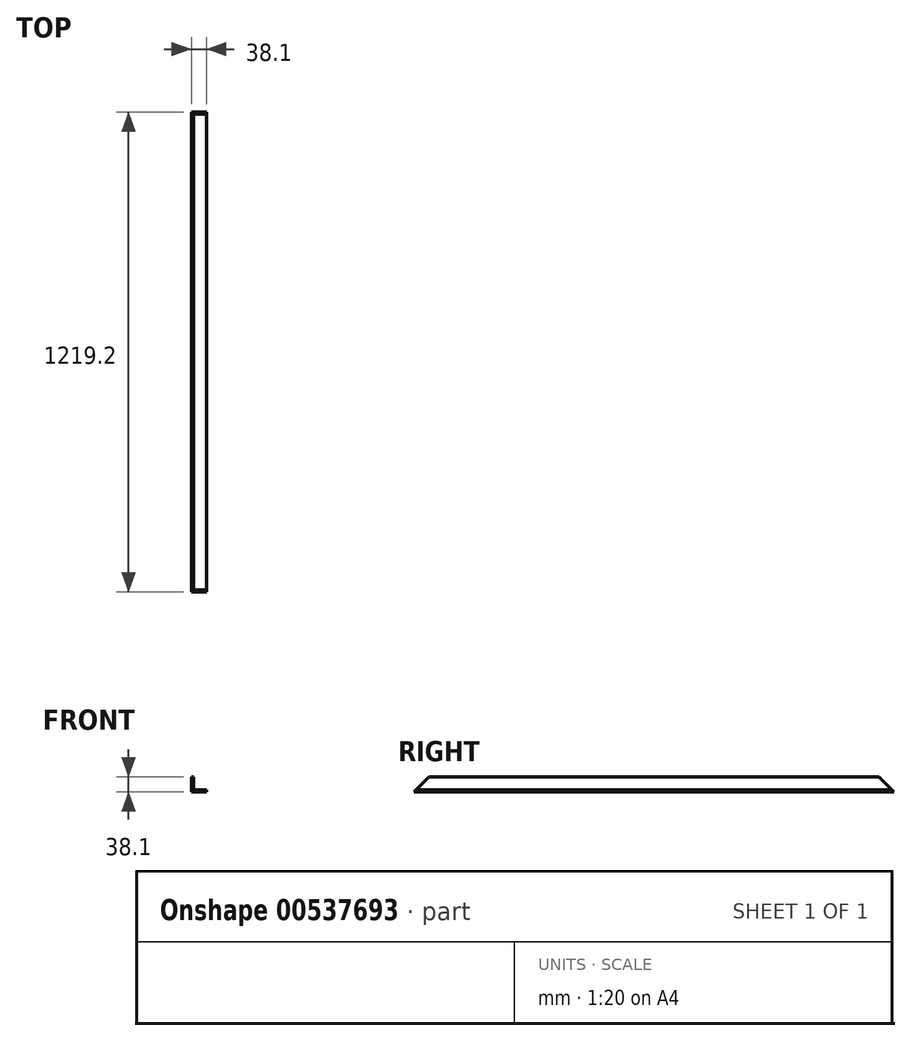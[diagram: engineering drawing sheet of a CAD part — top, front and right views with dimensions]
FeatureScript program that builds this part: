
annotation { "Feature Type Name" : "Feature", "Feature Type Description" : "" }
export const myFeature = defineFeature(function(context is Context, id is Id, definition is map)
    precondition{}
    {
        {
            var Q0;
            Q0=qCreatedBy(makeId("Front.planeOp"),FACE);
            var sketch = newSketch(context, id + "F0", { "sketchPlane" : qUnion([Q0])});
            skLineSegment(sketch, "E0", {"start": v(0, 0) * mm, "end": v(0, 38.1) * mm});
            skLineSegment(sketch, "E1", {"start": v(0, 38.1) * mm, "end": v(4.76, 38.1) * mm});
            skLineSegment(sketch, "E2", {"start": v(4.76, 38.1) * mm, "end": v(4.76, 4.76) * mm});
            skLineSegment(sketch, "E3", {"start": v(4.76, 4.76) * mm, "end": v(38.1, 4.76) * mm});
            skLineSegment(sketch, "E4", {"start": v(38.1, 4.76) * mm, "end": v(38.1, 0) * mm});
            skLineSegment(sketch, "E5", {"start": v(38.1, 0) * mm, "end": v(0, 0) * mm});
            skSolve(sketch);
        }
        {
            var Q0;
            Q0 = qSketchRegion(id + "F0", true);
            extrude(context, id + "F1", {"entities" : qUnion([Q0]), "depth" : 1219.2 * mm, "offsetDistance" : 25.4 * mm});
        }
        {
            var Q0;
            Q0=makeQuery(id+"F1.opExtrude","SWEPT_FACE",FACE,{"disambiguationData":[OSD([sQuery(id+"F0.wireOp",EDGE,"E0")])]});
            var sketch = newSketch(context, id + "F2", { "sketchPlane" : qUnion([Q0])});
            skLineSegment(sketch, "E6.0", {"start": v(1219.2, 0) * mm, "end": v(1219.2, 38.1) * mm});
            skLineSegment(sketch, "E6.1", {"start": v(1219.2, 38.1) * mm, "end": v(0, 38.1) * mm});
            skLineSegment(sketch, "E6.2", {"start": v(0, 0) * mm, "end": v(0, 38.1) * mm});
            skLineSegment(sketch, "E7", {"start": v(0, 0) * mm, "end": v(38.1, 38.1) * mm});
            skLineSegment(sketch, "E8", {"start": v(1219.2, 0) * mm, "end": v(1181.1, 38.1) * mm});
            skSolve(sketch);
        }
        {
            var Q0;
            Q0 = qSketchRegion(id + "F2", true);
            extrude(context, id + "F3", {"entities" : qUnion([Q0]), "operationType" : NewBodyOperationType.REMOVE, "endBound" : BoundingType.THROUGH_ALL, "oppositeDirection" : true, "depth" : 25.4 * mm, "offsetDistance" : 25.4 * mm});
        }
    });
